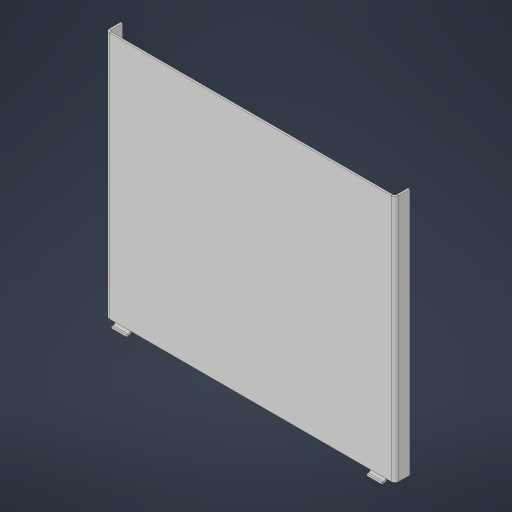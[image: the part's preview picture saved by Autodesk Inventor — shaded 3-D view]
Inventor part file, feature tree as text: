
AUTODESK INVENTOR PART (.ipt)
format: ipt  version: 2023.4 (Build 274418000, 418)  size: 224,256 bytes
history: native  units: in
note: dims shown in document units (in); Inventor stores cm internally (conversion verified against a paired STEP export)
features: sheet_metal_op x7, sketch x3, other x3, projected_geometry x1
ambient origin geometry x8: Origin, YZ Plane, XZ Plane, XY Plane, X Axis, Y Axis, Z Axis, Center Point
bodies: Solid1 (feature_tree)
feature tree (14):
  sheet_metal_op  "Face1"
  sheet_metal_op  "Flange1"
  sketch  "Sketch3"  dims[d2=0.12in d3=0.12in d4=0.06in d5=0.24in d6=0.12in d7=1.0in d8=90.0deg d9=0.12in d10=0.48in d11=0.12in d12=0.12in d13=0.375in d14=1.0in d15=8.0in d16=8.0in d17=1.0in d18=0.12in d19=0.12in d20=0.06in d21=0.24in d22=0.12in d23=0.25in d24=0.12in d25=0.06in d26=0.24in d27=0.12in d28=90.0deg d29=0.12in]
  sheet_metal_op  "Face2"
  sheet_metal_op  "Fold1"
  sketch  "Sketch1"  dims[d0=19.25in]
  other  "Plate1"
  sketch  "Sketch2"  dims[d1=16.5in]
  other  "Plate2"
  sheet_metal_op  "Bend1"
  sheet_metal_op  "Corner1"
  other  "Plate3"
  sheet_metal_op  "Bend2"
  projected_geometry  "Project Cut Edges1"
